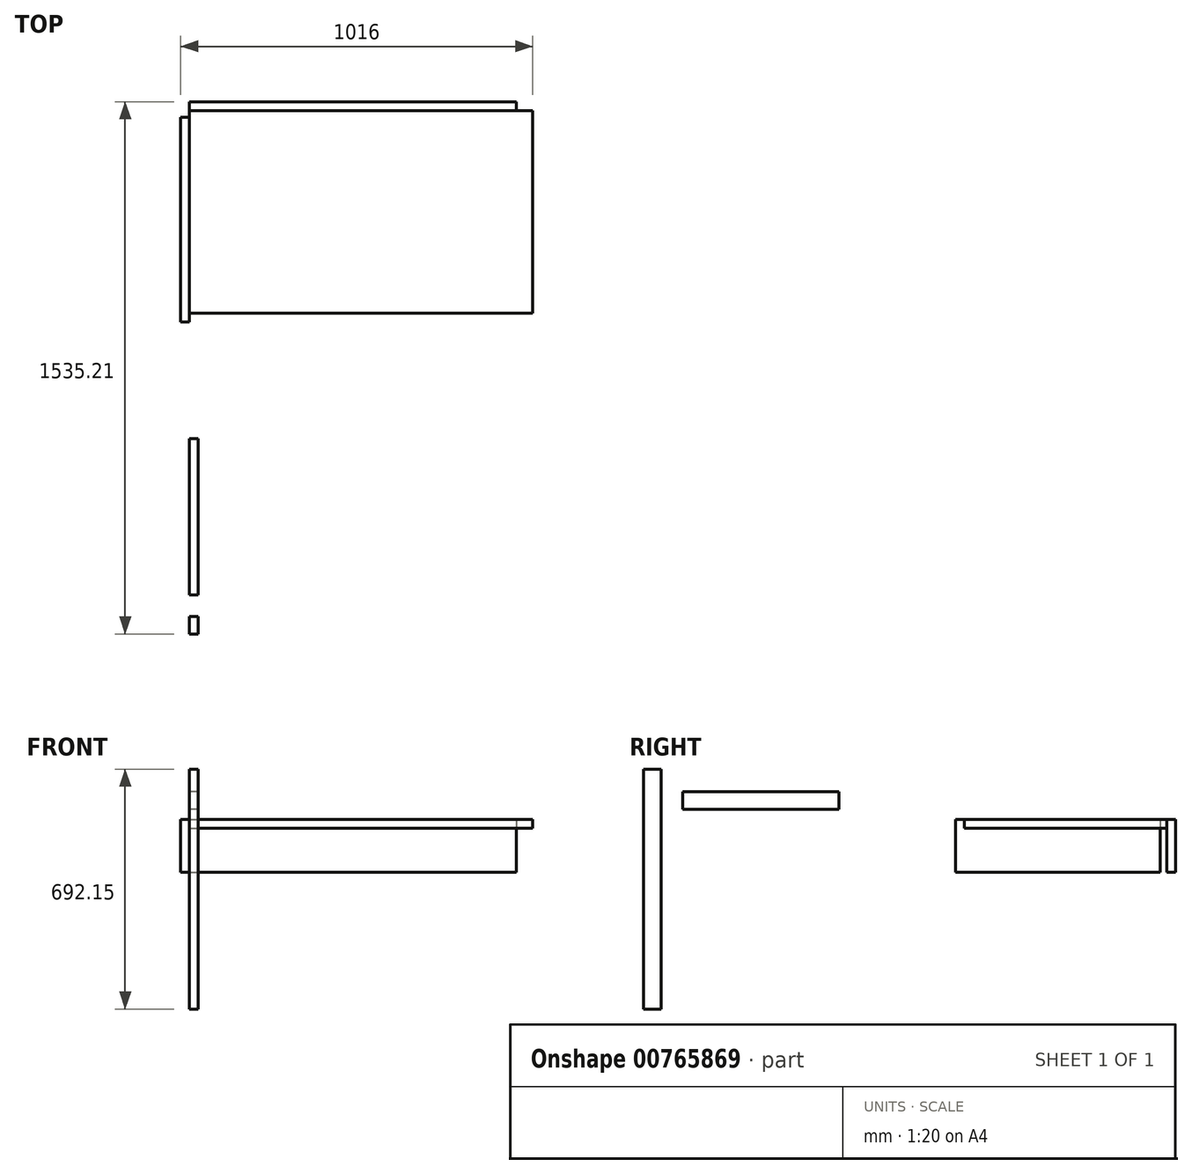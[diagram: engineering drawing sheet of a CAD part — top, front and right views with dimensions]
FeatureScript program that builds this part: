
annotation { "Feature Type Name" : "Feature", "Feature Type Description" : "" }
export const myFeature = defineFeature(function(context is Context, id is Id, definition is map)
    precondition{}
    {
        {
            var Q0;
            Q0=qCreatedBy(makeId("Top.planeOp"),FACE);
            var sketch = newSketch(context, id + "F0", { "sketchPlane" : qUnion([Q0])});
            skLineSegment(sketch, "E0.bottom", {"start": v(0, 0) * mm, "end": v(990.6, 0) * mm});
            skLineSegment(sketch, "E0.top", {"start": v(0, -584.2) * mm, "end": v(990.6, -584.2) * mm});
            skLineSegment(sketch, "E0.left", {"start": v(0, 0) * mm, "end": v(0, -584.2) * mm});
            skLineSegment(sketch, "E0.right", {"start": v(990.6, 0) * mm, "end": v(990.6, -584.2) * mm});
            skLineSegment(sketch, "E1.0", {"start": v(-25.4, 0) * mm, "end": v(-25.4, -584.2) * mm, "construction": true});
            skLineSegment(sketch, "E2.0", {"start": v(0, -609.6) * mm, "end": v(990.6, -609.6) * mm, "construction": true});
            skLineSegment(sketch, "E3.0", {"start": v(1016, 0) * mm, "end": v(1016, -584.2) * mm, "construction": true});
            skLineSegment(sketch, "E4.0", {"start": v(0, 25.4) * mm, "end": v(990.6, 25.4) * mm, "construction": true});
            skSolve(sketch);
        }
        {
            var Q0;
            Q0=qCreatedBy(makeId("Front.planeOp"),FACE);
            var sketch = newSketch(context, id + "F1", { "sketchPlane" : qUnion([Q0])});
            skLineSegment(sketch, "E5.bottom", {"start": v(0, 0) * mm, "end": v(942.98, 0) * mm});
            skLineSegment(sketch, "E5.top", {"start": v(0, -152.4) * mm, "end": v(942.98, -152.4) * mm});
            skLineSegment(sketch, "E5.left", {"start": v(0, 0) * mm, "end": v(0, -152.4) * mm});
            skLineSegment(sketch, "E5.right", {"start": v(942.98, 0) * mm, "end": v(942.98, -152.4) * mm});
            skSolve(sketch);
        }
        {
            var Q0;
            Q0=qCreatedBy(makeId("Right.planeOp"),FACE);
            var sketch = newSketch(context, id + "F2", { "sketchPlane" : qUnion([Q0])});
            skLineSegment(sketch, "E6.bottom", {"start": v(-19.05, 0) * mm, "end": v(-609.6, 0) * mm});
            skLineSegment(sketch, "E6.top", {"start": v(-19.05, -152.4) * mm, "end": v(-609.6, -152.4) * mm});
            skLineSegment(sketch, "E6.left", {"start": v(-19.05, 0) * mm, "end": v(-19.05, -152.4) * mm});
            skLineSegment(sketch, "E6.right", {"start": v(-609.6, 0) * mm, "end": v(-609.6, -152.4) * mm});
            skSolve(sketch);
        }
        {
            var Q0;
            Q0 = qSketchRegion(id + "F1", true);
            extrude(context, id + "F3", {"entities" : qUnion([Q0]), "oppositeDirection" : true, "depth" : 25.4 * mm, "offsetDistance" : 25.4 * mm});
        }
        {
            var Q0;
            Q0 = qSketchRegion(id + "F0", true);
            extrude(context, id + "F4", {"entities" : qUnion([Q0]), "oppositeDirection" : true, "depth" : 25.4 * mm, "offsetDistance" : 25.4 * mm});
        }
        {
            var Q0;
            Q0=makeQuery(id+"F2.imprint","IMPRINT",FACE,{"disambiguationData":[TD([[makeQuery(id+"F2.imprint","IMPRINT",EDGE,{"derivedFrom":sQuery(id+"F2.wireOp",EDGE,"E6.bottom")}),1.0]])]});
            extrude(context, id + "F5", {"entities" : qUnion([Q0]), "oppositeDirection" : true, "depth" : 25.4 * mm, "offsetDistance" : 25.4 * mm});
        }
        {
            var Q0;
            Q0=qCreatedBy(makeId("Right.planeOp"),FACE);
            var sketch = newSketch(context, id + "F6", { "sketchPlane" : qUnion([Q0])});
            skLineSegment(sketch, "E7.bottom", {"start": v(-1509.81, 145.62) * mm, "end": v(-1459.01, 145.62) * mm});
            skLineSegment(sketch, "E7.top", {"start": v(-1509.81, -546.53) * mm, "end": v(-1459.01, -546.53) * mm});
            skLineSegment(sketch, "E7.left", {"start": v(-1509.81, 145.62) * mm, "end": v(-1509.81, -546.53) * mm});
            skLineSegment(sketch, "E7.right", {"start": v(-1459.01, 145.62) * mm, "end": v(-1459.01, -546.53) * mm});
            skSolve(sketch);
        }
        {
            var Q0;
            Q0 = qSketchRegion(id + "F6", true);
            extrude(context, id + "F7", {"entities" : qUnion([Q0]), "depth" : 25.4 * mm, "offsetDistance" : 25.4 * mm});
        }
        {
            var Q0;
            Q0=qCreatedBy(makeId("Right.planeOp"),FACE);
            var sketch = newSketch(context, id + "F8", { "sketchPlane" : qUnion([Q0])});
            skLineSegment(sketch, "E8.bottom", {"start": v(-1397.22, 80.92) * mm, "end": v(-946.37, 80.92) * mm});
            skLineSegment(sketch, "E8.top", {"start": v(-1397.22, 30.12) * mm, "end": v(-946.37, 30.12) * mm});
            skLineSegment(sketch, "E8.left", {"start": v(-1397.22, 80.92) * mm, "end": v(-1397.22, 30.12) * mm});
            skLineSegment(sketch, "E8.right", {"start": v(-946.37, 80.92) * mm, "end": v(-946.37, 30.12) * mm});
            skSolve(sketch);
        }
        {
            var Q0;
            Q0 = qSketchRegion(id + "F8", true);
            extrude(context, id + "F9", {"entities" : qUnion([Q0]), "depth" : 25.4 * mm, "offsetDistance" : 25.4 * mm});
        }
    });
